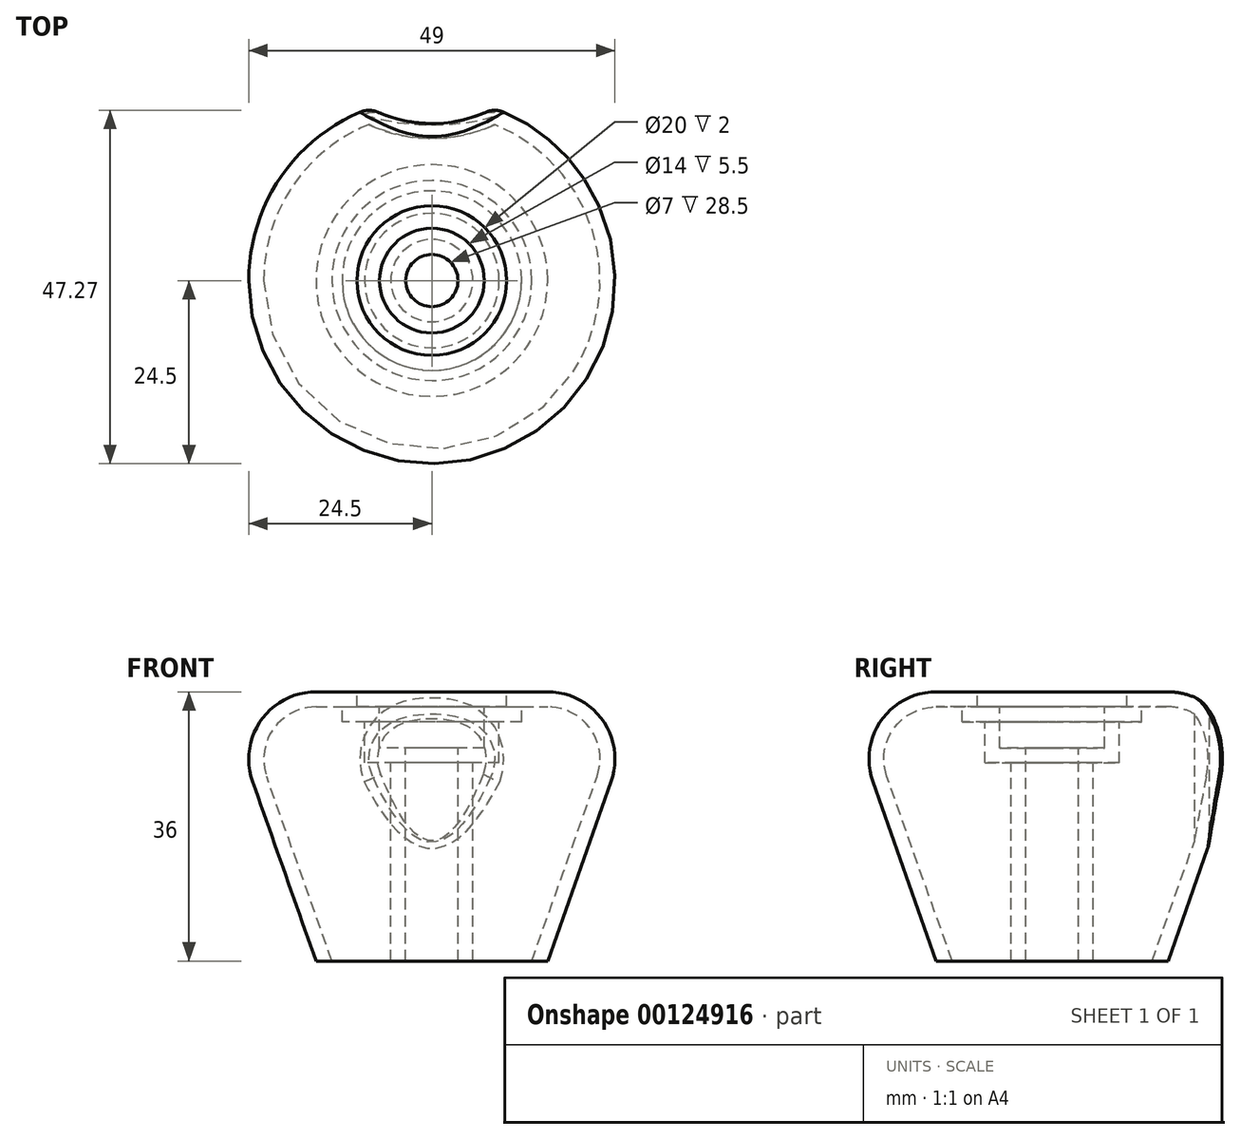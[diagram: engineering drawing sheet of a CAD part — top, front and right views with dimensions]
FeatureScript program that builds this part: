
annotation { "Feature Type Name" : "Feature", "Feature Type Description" : "" }
export const myFeature = defineFeature(function(context is Context, id is Id, definition is map)
    precondition{}
    {
        {
            var Q0;
            Q0=qCreatedBy(makeId("Front.planeOp"),FACE);
            var sketch = newSketch(context, id + "F0", { "sketchPlane" : qUnion([Q0])});
            skLineSegment(sketch, "E0", {"start": v(0, 0) * mm, "end": v(0, 36) * mm});
            skLineSegment(sketch, "E1", {"start": v(0, 36) * mm, "end": v(-28.23, 36) * mm});
            skLineSegment(sketch, "E2", {"start": v(-28.23, 36) * mm, "end": v(-15.5, 0) * mm});
            skLineSegment(sketch, "E3", {"start": v(-15.5, 0) * mm, "end": v(0, 0) * mm});
            skArc(sketch, "E4", {"start": v(-15.5, 36) * mm, "mid": v(-22.85, 32.2) * mm, "end": v(-23.99, 24) * mm});
            skLineSegment(sketch, "E5", {"start": v(-24.5, 33.01) * mm, "end": v(-24.5, 13.34) * mm});
            skSolve(sketch);
        }
        {
            var Q0;
            {var subQ5=sQuery(id+"F0.wireOp",EDGE,"E0");Q0=makeQuery(id+"F0.imprint","IMPRINT",FACE,{"disambiguationData":[TD([[makeQuery(id+"F0.imprint","IMPRINT",EDGE,{"derivedFrom":subQ5}),1.0]])]});}
            var Q1;
            Q1=sQuery(id+"F0.wireOp",EDGE,"E0");
            revolve(context, id + "F1", {"entities" : qUnion([Q0]), "axis" : qUnion([Q1]), "revolveType" : RevolveType.FULL});
        }
        {
            var Q0;
            Q0=qCreatedBy(makeId("Top.planeOp"),FACE);
            var sketch = newSketch(context, id + "F2", { "sketchPlane" : qUnion([Q0])});
            skArc(sketch, "E6", {"start": v(-14.63, 28.52) * mm, "mid": v(0.4, 21) * mm, "end": v(15.08, 29.17) * mm});
            skLineSegment(sketch, "E7", {"start": v(-14.63, 28.52) * mm, "end": v(0, 39) * mm});
            skLineSegment(sketch, "E8", {"start": v(15.08, 29.17) * mm, "end": v(0, 39) * mm});
            skLineSegment(sketch, "E9", {"start": v(0, 39) * mm, "end": v(0, 0) * mm});
            skSolve(sketch);
        }
        {
            var Q0;
            {var subQ0=sQuery(id+"F2.wireOp",EDGE,"E7");Q0=makeQuery(id+"F2.imprint","IMPRINT",FACE,{"disambiguationData":[TD([[makeQuery(id+"F2.imprint","IMPRINT",EDGE,{"derivedFrom":subQ0}),-1.0]])]});}
            var Q1;
            {var subQ0=sQuery(id+"F2.wireOp",EDGE,"E8");Q1=makeQuery(id+"F2.imprint","IMPRINT",FACE,{"disambiguationData":[TD([[makeQuery(id+"F2.imprint","IMPRINT",EDGE,{"derivedFrom":subQ0}),1.0]])]});}
            extrude(context, id + "F3", {"entities" : qUnion([Q0, Q1]), "operationType" : NewBodyOperationType.REMOVE, "endBound" : BoundingType.THROUGH_ALL, "depth" : 25 * mm});
        }
        {
            var Q0;
            Q0=makeQuery(id+"F1.opRevolve","SWEPT_FACE",FACE,{"disambiguationData":[OSD([sQuery(id+"F0.wireOp",EDGE,"E1")])]});
            var sketch = newSketch(context, id + "F4", { "sketchPlane" : qUnion([Q0])});
            skCircle(sketch, "E10", {"center": v(0, 0) * mm, "radius": 10 * mm});
            skSolve(sketch);
        }
        {
            var Q0;
            Q0=makeQuery(id+"F4.imprint","IMPRINT",FACE,{"disambiguationData":[TD([[makeQuery(id+"F4.imprint","IMPRINT",EDGE,{"derivedFrom":sQuery(id+"F4.wireOp",EDGE,"E10")}),1.0]])]});
            extrude(context, id + "F5", {"entities" : qUnion([Q0]), "operationType" : NewBodyOperationType.REMOVE, "oppositeDirection" : true, "depth" : 2 * mm});
        }
        {
            var Q0;
            Q0=makeQuery(id+"F5.boolean.opBoolean","COPY",FACE,{"derivedFrom":makeQuery(id+"F5.opExtrude","CAP_FACE",FACE,{"disambiguationData":[OSD([sQuery(id+"F4.wireOp",EDGE,"E10")])],"isStart":false})});
            var sketch = newSketch(context, id + "F6", { "sketchPlane" : qUnion([Q0])});
            skCircle(sketch, "E11", {"center": v(0, 0) * mm, "radius": 7 * mm});
            skSolve(sketch);
        }
        {
            var Q0;
            Q0=makeQuery(id+"F6.imprint","IMPRINT",FACE,{"disambiguationData":[TD([[makeQuery(id+"F6.imprint","IMPRINT",EDGE,{"derivedFrom":sQuery(id+"F6.wireOp",EDGE,"E11")}),1.0]])]});
            extrude(context, id + "F7", {"entities" : qUnion([Q0]), "operationType" : NewBodyOperationType.REMOVE, "oppositeDirection" : true, "depth" : 5.5 * mm});
        }
        {
            var Q0;
            Q0=makeQuery(id+"F7.boolean.opBoolean","COPY",FACE,{"derivedFrom":makeQuery(id+"F7.opExtrude","CAP_FACE",FACE,{"disambiguationData":[OSD([sQuery(id+"F6.wireOp",EDGE,"E11")])],"isStart":false})});
            var sketch = newSketch(context, id + "F8", { "sketchPlane" : qUnion([Q0])});
            skCircle(sketch, "E12", {"center": v(0, 0) * mm, "radius": 3.5 * mm});
            skSolve(sketch);
        }
        {
            var Q0;
            Q0 = qSketchRegion(id + "F8", true);
            extrude(context, id + "F9", {"entities" : qUnion([Q0]), "operationType" : NewBodyOperationType.REMOVE, "endBound" : BoundingType.THROUGH_ALL, "oppositeDirection" : true, "depth" : 25 * mm});
        }
        {
            var Q0;
            Q0=makeQuery(id+"F1.opRevolve","SWEPT_FACE",FACE,{"disambiguationData":[OSD([sQuery(id+"F0.wireOp",EDGE,"E3")])]});
            shell(context, id + "F10", {"entities" : qUnion([Q0]), "thickness" : 2 * mm});
        }
        {
            var Q0;
            Q0=makeQuery(id+"FsEg5nOM3woyhCO_1.4.F3.boolean.opBoolean","INTERSECT",EDGE,{"derivedFrom":[makeQuery(id+"F1.opRevolve","SWEPT_FACE",FACE,{"disambiguationData":[OSD([sQuery(id+"F0.wireOp",EDGE,"E4")])]}),makeQuery(id+"FsEg5nOM3woyhCO_1.4.F3.opExtrude","SWEPT_FACE",FACE,{"disambiguationData":[OSD([sQuery(id+"F2.wireOp",EDGE,"E6")])]})]});
            var Q1;
            Q1=makeQuery(id+"FsEg5nOM3woyhCO_1.5.F3.boolean.opBoolean","INTERSECT",EDGE,{"derivedFrom":[makeQuery(id+"F1.opRevolve","SWEPT_FACE",FACE,{"disambiguationData":[OSD([sQuery(id+"F0.wireOp",EDGE,"E4")])]}),makeQuery(id+"FsEg5nOM3woyhCO_1.5.F3.opExtrude","SWEPT_FACE",FACE,{"disambiguationData":[OSD([sQuery(id+"F2.wireOp",EDGE,"E6")])]})]});
            var Q2;
            Q2=makeQuery(id+"FsEg5nOM3woyhCO_1.6.F3.boolean.opBoolean","INTERSECT",EDGE,{"derivedFrom":[makeQuery(id+"F1.opRevolve","SWEPT_FACE",FACE,{"disambiguationData":[OSD([sQuery(id+"F0.wireOp",EDGE,"E4")])]}),makeQuery(id+"FsEg5nOM3woyhCO_1.6.F3.opExtrude","SWEPT_FACE",FACE,{"disambiguationData":[OSD([sQuery(id+"F2.wireOp",EDGE,"E6")])]})]});
            var Q3;
            Q3=makeQuery(id+"F3.boolean.opBoolean","INTERSECT",EDGE,{"derivedFrom":[makeQuery(id+"F1.opRevolve","SWEPT_FACE",FACE,{"disambiguationData":[OSD([sQuery(id+"F0.wireOp",EDGE,"E4")])]}),makeQuery(id+"F3.opExtrude","SWEPT_FACE",FACE,{"disambiguationData":[OSD([sQuery(id+"F2.wireOp",EDGE,"E6")])]})]});
            var Q4;
            Q4=makeQuery(id+"FsEg5nOM3woyhCO_1.1.F3.boolean.opBoolean","INTERSECT",EDGE,{"derivedFrom":[makeQuery(id+"F1.opRevolve","SWEPT_FACE",FACE,{"disambiguationData":[OSD([sQuery(id+"F0.wireOp",EDGE,"E4")])]}),makeQuery(id+"FsEg5nOM3woyhCO_1.1.F3.opExtrude","SWEPT_FACE",FACE,{"disambiguationData":[OSD([sQuery(id+"F2.wireOp",EDGE,"E6")])]})]});
            var Q5;
            Q5=makeQuery(id+"FsEg5nOM3woyhCO_1.2.F3.boolean.opBoolean","INTERSECT",EDGE,{"derivedFrom":[makeQuery(id+"F1.opRevolve","SWEPT_FACE",FACE,{"disambiguationData":[OSD([sQuery(id+"F0.wireOp",EDGE,"E4")])]}),makeQuery(id+"FsEg5nOM3woyhCO_1.2.F3.opExtrude","SWEPT_FACE",FACE,{"disambiguationData":[OSD([sQuery(id+"F2.wireOp",EDGE,"E6")])]})]});
            var Q6;
            Q6=makeQuery(id+"FsEg5nOM3woyhCO_1.3.F3.boolean.opBoolean","INTERSECT",EDGE,{"derivedFrom":[makeQuery(id+"F1.opRevolve","SWEPT_FACE",FACE,{"disambiguationData":[OSD([sQuery(id+"F0.wireOp",EDGE,"E4")])]}),makeQuery(id+"FsEg5nOM3woyhCO_1.3.F3.opExtrude","SWEPT_FACE",FACE,{"disambiguationData":[OSD([sQuery(id+"F2.wireOp",EDGE,"E6")])]})]});
            fillet(context, id + "F11", {"entities" : qUnion([Q0, Q1, Q2, Q3, Q4, Q5, Q6]), "radius" : 3 * mm, "tangentPropagation" : true, "allowEdgeOverflow" : false});
        }
    });
